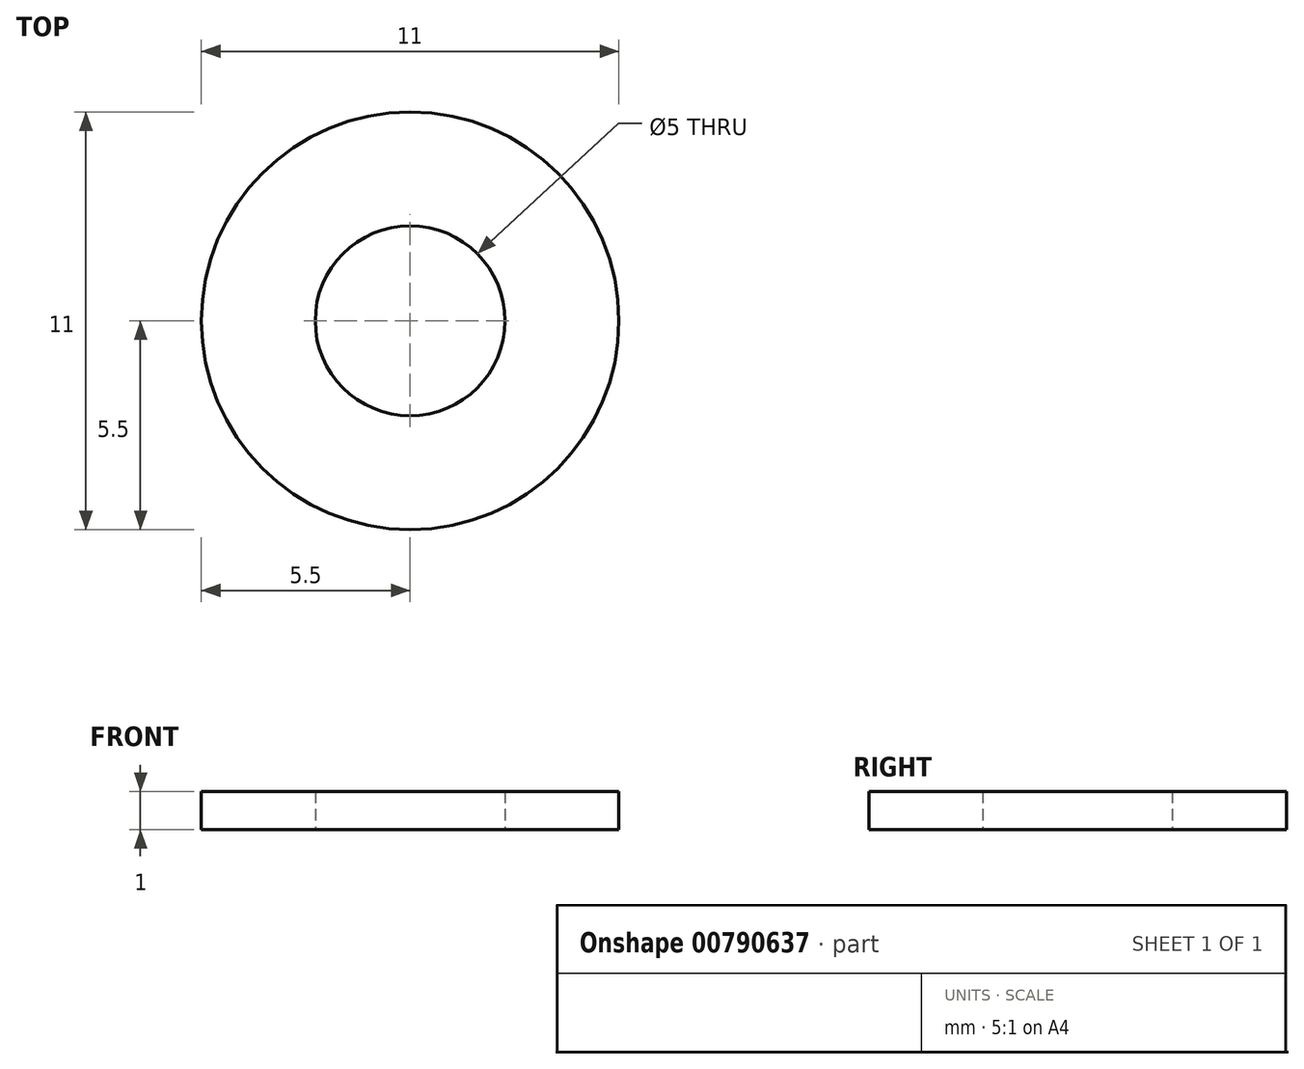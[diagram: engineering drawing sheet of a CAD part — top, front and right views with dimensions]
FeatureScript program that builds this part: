
annotation { "Feature Type Name" : "Feature", "Feature Type Description" : "" }
export const myFeature = defineFeature(function(context is Context, id is Id, definition is map)
    precondition{}
    {
        {
            var Q0;
            Q0=qCreatedBy(makeId("Top.planeOp"),FACE);
            var sketch = newSketch(context, id + "F0", { "sketchPlane" : qUnion([Q0])});
            skCircle(sketch, "E0", {"center": v(0, 0) * mm, "radius": 2.5 * mm});
            skCircle(sketch, "E1.0", {"center": v(0, 0) * mm, "radius": 5.5 * mm});
            skSolve(sketch);
        }
        {
            var Q0;
            Q0=makeQuery(id+"F0.imprint","IMPRINT",FACE,{"disambiguationData":[TD([[makeQuery(id+"F0.imprint","IMPRINT",EDGE,{"derivedFrom":sQuery(id+"F0.wireOp",EDGE,"E0")}),-1.0]])]});
            extrude(context, id + "F1", {"entities" : qUnion([Q0]), "depth" : 1 * mm, "offsetDistance" : 25 * mm});
        }
    });
